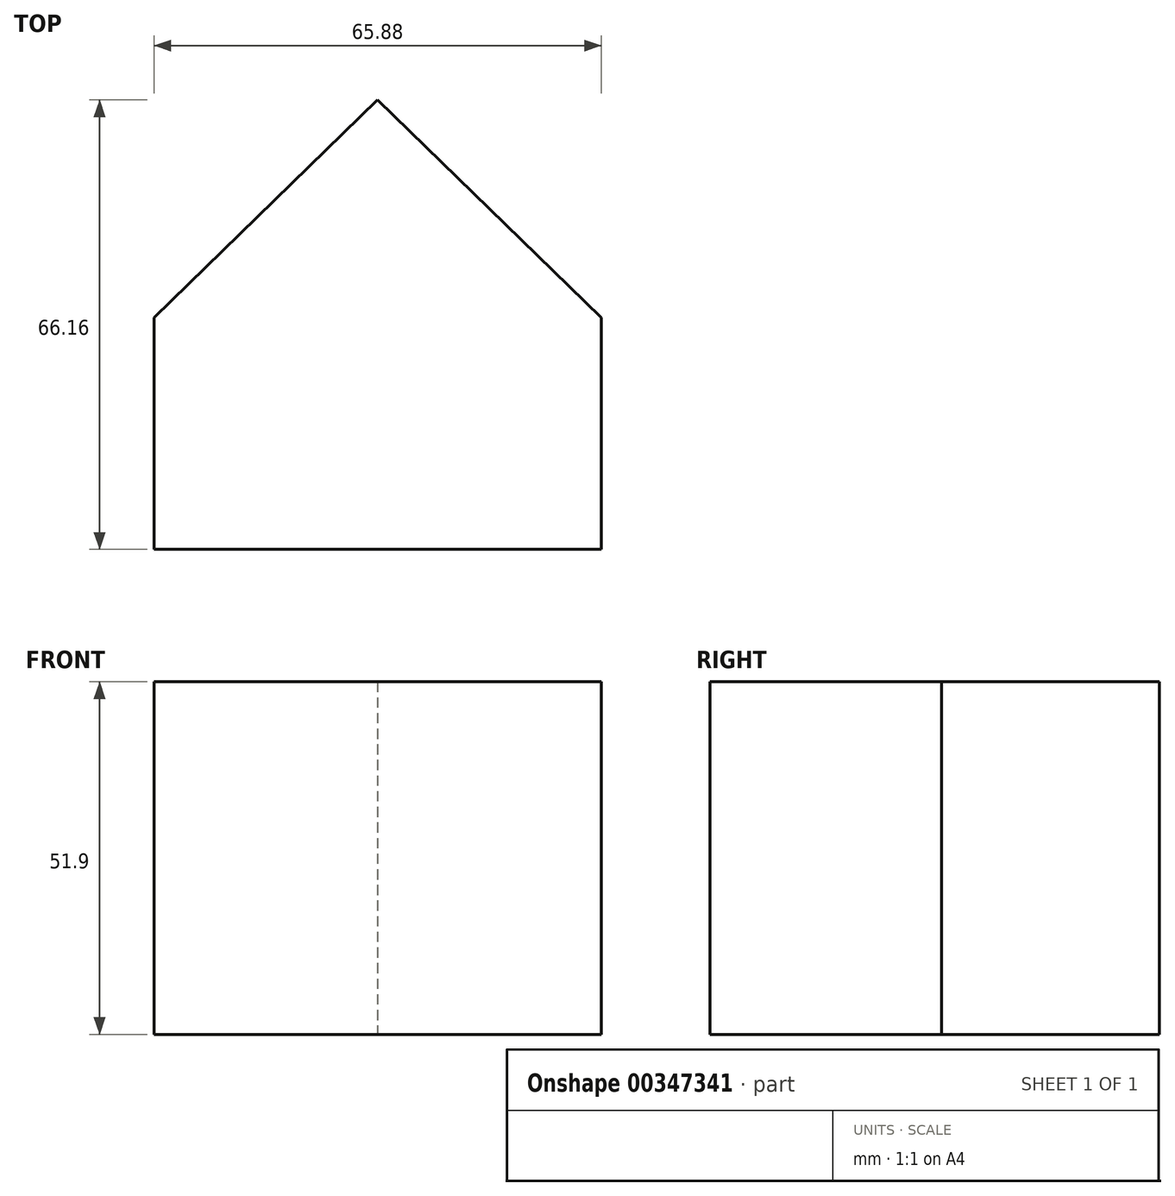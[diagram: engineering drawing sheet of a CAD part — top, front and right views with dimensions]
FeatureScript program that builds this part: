
annotation { "Feature Type Name" : "Feature", "Feature Type Description" : "" }
export const myFeature = defineFeature(function(context is Context, id is Id, definition is map)
    precondition{}
    {
        {
            var Q0;
            Q0=qCreatedBy(makeId("Top.planeOp"),FACE);
            var sketch = newSketch(context, id + "F0", { "sketchPlane" : qUnion([Q0])});
            skLineSegment(sketch, "E0.bottom", {"start": v(32.94, 17.05) * mm, "end": v(-32.94, 17.05) * mm});
            skLineSegment(sketch, "E0.top", {"start": v(32.94, -17.05) * mm, "end": v(-32.94, -17.05) * mm});
            skLineSegment(sketch, "E0.left", {"start": v(32.94, 17.05) * mm, "end": v(32.94, -17.05) * mm});
            skLineSegment(sketch, "E0.right", {"start": v(-32.94, 17.05) * mm, "end": v(-32.94, -17.05) * mm});
            skPoint(sketch, "E0.middle", {"position": v(0, 0) * mm});
            skLineSegment(sketch, "E1", {"start": v(-32.94, 17.05) * mm, "end": v(0, 49.11) * mm});
            skLineSegment(sketch, "E2", {"start": v(0, 49.11) * mm, "end": v(32.94, 17.05) * mm});
            skSolve(sketch);
        }
        {
            var Q0;
            Q0=makeQuery(id+"F0.imprint","IMPRINT",FACE,{"disambiguationData":[TD([[makeQuery(id+"F0.imprint","IMPRINT",EDGE,{"derivedFrom":sQuery(id+"F0.wireOp",EDGE,"E0.bottom")}),-1.0]])]});
            var Q1;
            Q1=makeQuery(id+"F0.imprint","IMPRINT",FACE,{"disambiguationData":[TD([[makeQuery(id+"F0.imprint","IMPRINT",EDGE,{"derivedFrom":sQuery(id+"F0.wireOp",EDGE,"E0.bottom")}),1.0]])]});
            extrude(context, id + "F1", {"entities" : qUnion([Q0, Q1]), "depth" : 51.9 * mm});
        }
    });
